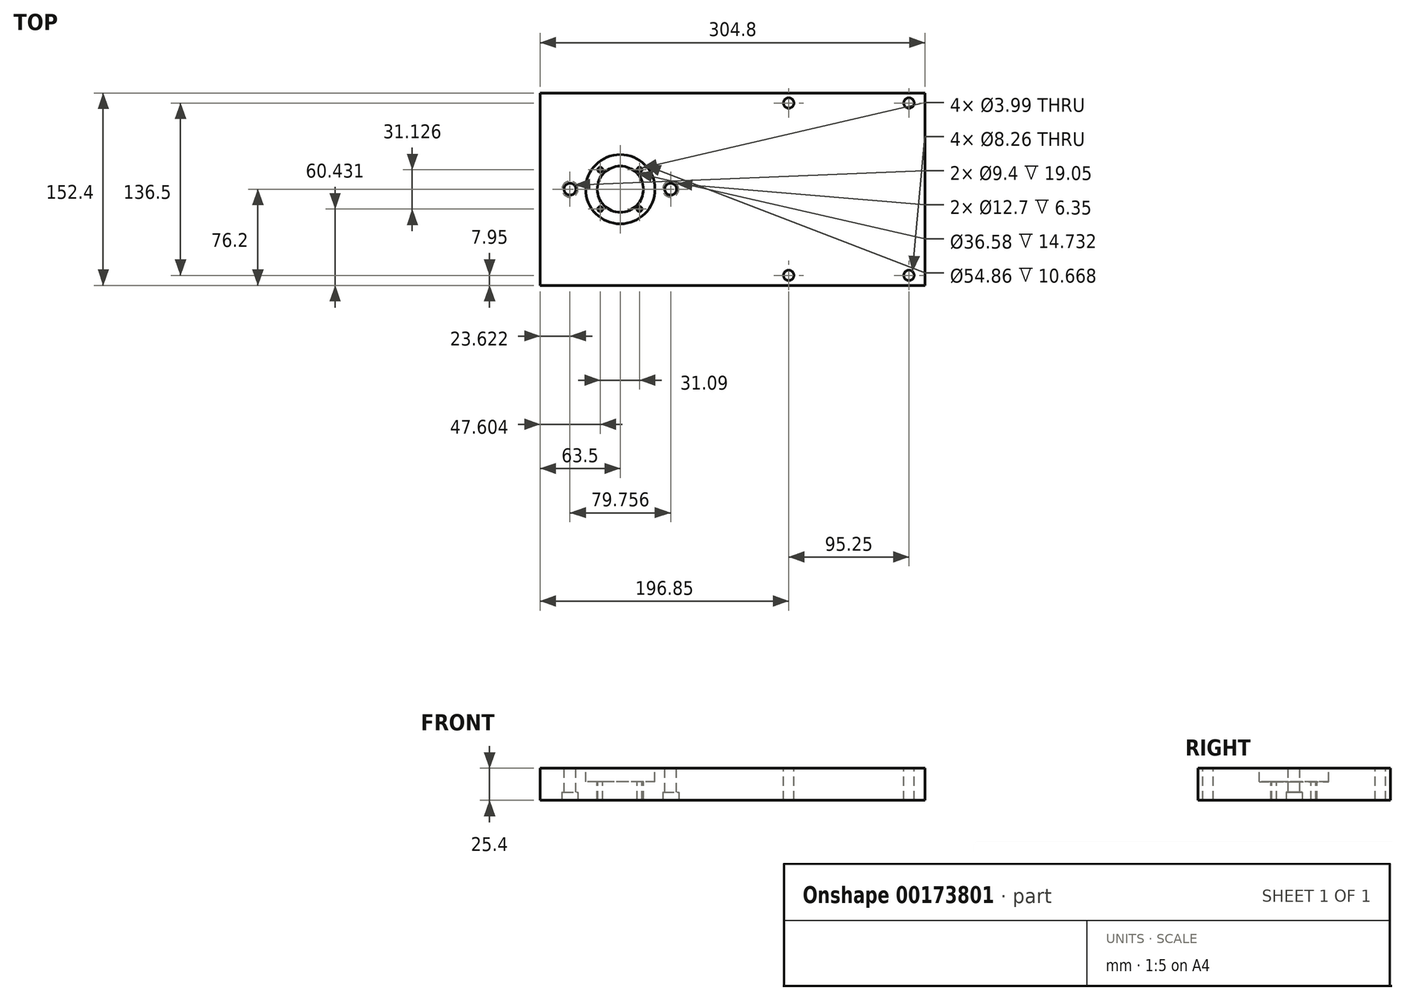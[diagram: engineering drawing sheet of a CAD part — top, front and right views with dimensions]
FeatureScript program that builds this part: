
annotation { "Feature Type Name" : "Feature", "Feature Type Description" : "" }
export const myFeature = defineFeature(function(context is Context, id is Id, definition is map)
    precondition{}
    {
        {
            var Q0;
            Q0=qCreatedBy(makeId("Top.planeOp"),FACE);
            var sketch = newSketch(context, id + "F0", { "sketchPlane" : qUnion([Q0])});
            skLineSegment(sketch, "E0.bottom", {"start": v(-152.4, 76.2) * mm, "end": v(152.4, 76.2) * mm});
            skLineSegment(sketch, "E0.top", {"start": v(-152.4, -76.2) * mm, "end": v(152.4, -76.2) * mm});
            skLineSegment(sketch, "E0.left", {"start": v(-152.4, 76.2) * mm, "end": v(-152.4, -76.2) * mm});
            skLineSegment(sketch, "E0.right", {"start": v(152.4, 76.2) * mm, "end": v(152.4, -76.2) * mm});
            skPoint(sketch, "E0.middle", {"position": v(0, 0) * mm});
            skSolve(sketch);
        }
        {
            var Q0;
            Q0 = qSketchRegion(id + "F0", true);
            extrude(context, id + "F1", {"entities" : qUnion([Q0]), "oppositeDirection" : true, "depth" : 25.4 * mm});
        }
        {
            var Q0;
            Q0=makeQuery(id+"F1.opExtrude","CAP_FACE",FACE,{"disambiguationData":[OSD([sQuery(id+"F0.wireOp",EDGE,"E0.bottom"),sQuery(id+"F0.wireOp",EDGE,"E0.top"),sQuery(id+"F0.wireOp",EDGE,"E0.left"),sQuery(id+"F0.wireOp",EDGE,"E0.right")])],"isStart":true});
            var sketch = newSketch(context, id + "F2", { "sketchPlane" : qUnion([Q0])});
            skCircle(sketch, "E1", {"center": v(-88.9, 0) * mm, "radius": 18.29 * mm});
            skSolve(sketch);
        }
        {
            var Q0;
            Q0 = qSketchRegion(id + "F2", true);
            extrude(context, id + "F3", {"entities" : qUnion([Q0]), "operationType" : NewBodyOperationType.REMOVE, "endBound" : BoundingType.THROUGH_ALL, "oppositeDirection" : true, "depth" : 25.4 * mm});
        }
        {
            var Q0;
            Q0=makeQuery(id+"F1.opExtrude","CAP_FACE",FACE,{"disambiguationData":[OSD([sQuery(id+"F0.wireOp",EDGE,"E0.bottom"),sQuery(id+"F0.wireOp",EDGE,"E0.top"),sQuery(id+"F0.wireOp",EDGE,"E0.left"),sQuery(id+"F0.wireOp",EDGE,"E0.right")])],"isStart":true});
            var sketch = newSketch(context, id + "F4", { "sketchPlane" : qUnion([Q0])});
            skCircle(sketch, "E2", {"center": v(-88.9, 0) * mm, "radius": 27.43 * mm});
            skSolve(sketch);
        }
        {
            var Q0;
            Q0 = qSketchRegion(id + "F4", true);
            extrude(context, id + "F5", {"entities" : qUnion([Q0]), "operationType" : NewBodyOperationType.REMOVE, "oppositeDirection" : true, "depth" : 10.67 * mm});
        }
        {
            var Q0;
            Q0=makeQuery(id+"F5.boolean.opBoolean","COPY",FACE,{"derivedFrom":makeQuery(id+"F5.opExtrude","CAP_FACE",FACE,{"disambiguationData":[OSD([sQuery(id+"F4.wireOp",EDGE,"E2")])],"isStart":false})});
            var sketch = newSketch(context, id + "F6", { "sketchPlane" : qUnion([Q0])});
            skCircle(sketch, "E3", {"center": v(-104.8, 15.36) * mm, "radius": 2 * mm});
            skCircle(sketch, "E4", {"center": v(-73.7, 15.36) * mm, "radius": 2 * mm});
            skCircle(sketch, "E5", {"center": v(-73.7, -15.77) * mm, "radius": 2 * mm});
            skCircle(sketch, "E6", {"center": v(-104.8, -15.77) * mm, "radius": 2 * mm});
            skSolve(sketch);
        }
        {
            var Q0;
            Q0=sQuery(id+"F6.wireOp",VERTEX,"E3.center");
            var Q1;
            Q1=sQuery(id+"F6.wireOp",VERTEX,"E6.center");
            var Q2;
            Q2=sQuery(id+"F6.wireOp",VERTEX,"E5.center");
            var Q3;
            Q3=sQuery(id+"F6.wireOp",VERTEX,"E4.center");
            var Q4;
            Q4=makeQuery(id+"F1.opExtrude","SWEPT_BODY",BODY,{"disambiguationData":[OSD([sQuery(id+"F0.wireOp",EDGE,"E0.bottom"),sQuery(id+"F0.wireOp",EDGE,"E0.top"),sQuery(id+"F0.wireOp",EDGE,"E0.left"),sQuery(id+"F0.wireOp",EDGE,"E0.right")])]});
            hole(context, id + "F7", {"style" : HoleStyle.SIMPLE, "endStyle" : HoleEndStyle.THROUGH, "holeDiameter" : 4 * mm, "locations" : qUnion([Q0, Q1, Q2, Q3]), "scope" : qUnion([Q4]), "isTappedThrough" : true});
        }
        {
            var Q0;
            Q0=makeQuery(id+"F1.opExtrude","CAP_FACE",FACE,{"disambiguationData":[OSD([sQuery(id+"F0.wireOp",EDGE,"E0.bottom"),sQuery(id+"F0.wireOp",EDGE,"E0.top"),sQuery(id+"F0.wireOp",EDGE,"E0.left"),sQuery(id+"F0.wireOp",EDGE,"E0.right")])],"isStart":true});
            var sketch = newSketch(context, id + "F8", { "sketchPlane" : qUnion([Q0])});
            skCircle(sketch, "E7", {"center": v(-49.02, 0) * mm, "radius": 4.7 * mm});
            skCircle(sketch, "E8", {"center": v(-128.78, 0) * mm, "radius": 4.7 * mm});
            skSolve(sketch);
        }
        {
            var Q0;
            Q0=makeQuery(id+"F8.imprint","IMPRINT",FACE,{"disambiguationData":[TD([[makeQuery(id+"F8.imprint","IMPRINT",EDGE,{"derivedFrom":sQuery(id+"F8.wireOp",EDGE,"E8")}),1.0]])]});
            var Q1;
            Q1=makeQuery(id+"F8.imprint","IMPRINT",FACE,{"disambiguationData":[TD([[makeQuery(id+"F8.imprint","IMPRINT",EDGE,{"derivedFrom":sQuery(id+"F8.wireOp",EDGE,"E7")}),1.0]])]});
            var Q2;
            Q2=sQuery(id+"F8.wireOp",EDGE,"E8");
            var Q3;
            Q3=sQuery(id+"F8.wireOp",EDGE,"E7");
            extrude(context, id + "F9", {"entities" : qUnion([Q0, Q1]), "operationType" : NewBodyOperationType.REMOVE, "surfaceEntities" : qUnion([Q2, Q3]), "endBound" : BoundingType.THROUGH_ALL, "oppositeDirection" : true, "depth" : 25.4 * mm});
        }
        {
            var Q0;
            Q0=makeQuery(id+"F1.opExtrude","CAP_FACE",FACE,{"disambiguationData":[OSD([sQuery(id+"F0.wireOp",EDGE,"E0.bottom"),sQuery(id+"F0.wireOp",EDGE,"E0.top"),sQuery(id+"F0.wireOp",EDGE,"E0.left"),sQuery(id+"F0.wireOp",EDGE,"E0.right")])],"isStart":false});
            var sketch = newSketch(context, id + "F10", { "sketchPlane" : qUnion([Q0])});
            skCircle(sketch, "E9", {"center": v(-128.78, 0) * mm, "radius": 6.35 * mm});
            skCircle(sketch, "E10", {"center": v(-49.02, 0) * mm, "radius": 6.35 * mm});
            skSolve(sketch);
        }
        {
            var Q0;
            Q0 = qSketchRegion(id + "F10", true);
            extrude(context, id + "F11", {"entities" : qUnion([Q0]), "operationType" : NewBodyOperationType.REMOVE, "oppositeDirection" : true, "depth" : 6.35 * mm});
        }
        {
            var Q0;
            Q0=makeQuery(id+"F1.opExtrude","CAP_FACE",FACE,{"disambiguationData":[OSD([sQuery(id+"F0.wireOp",EDGE,"E0.bottom"),sQuery(id+"F0.wireOp",EDGE,"E0.top"),sQuery(id+"F0.wireOp",EDGE,"E0.left"),sQuery(id+"F0.wireOp",EDGE,"E0.right")])],"isStart":true});
            var sketch = newSketch(context, id + "F12", { "sketchPlane" : qUnion([Q0])});
            skCircle(sketch, "E11", {"center": v(44.45, 68.25) * mm, "radius": 4.13 * mm});
            skCircle(sketch, "E12", {"center": v(139.7, 68.25) * mm, "radius": 4.13 * mm});
            skCircle(sketch, "E13", {"center": v(44.45, -68.25) * mm, "radius": 4.13 * mm});
            skCircle(sketch, "E14", {"center": v(139.7, -68.25) * mm, "radius": 4.13 * mm});
            skSolve(sketch);
        }
        {
            var Q0;
            Q0 = qSketchRegion(id + "F12", true);
            extrude(context, id + "F13", {"entities" : qUnion([Q0]), "operationType" : NewBodyOperationType.REMOVE, "endBound" : BoundingType.THROUGH_ALL, "oppositeDirection" : true, "depth" : 25.4 * mm});
        }
    });
